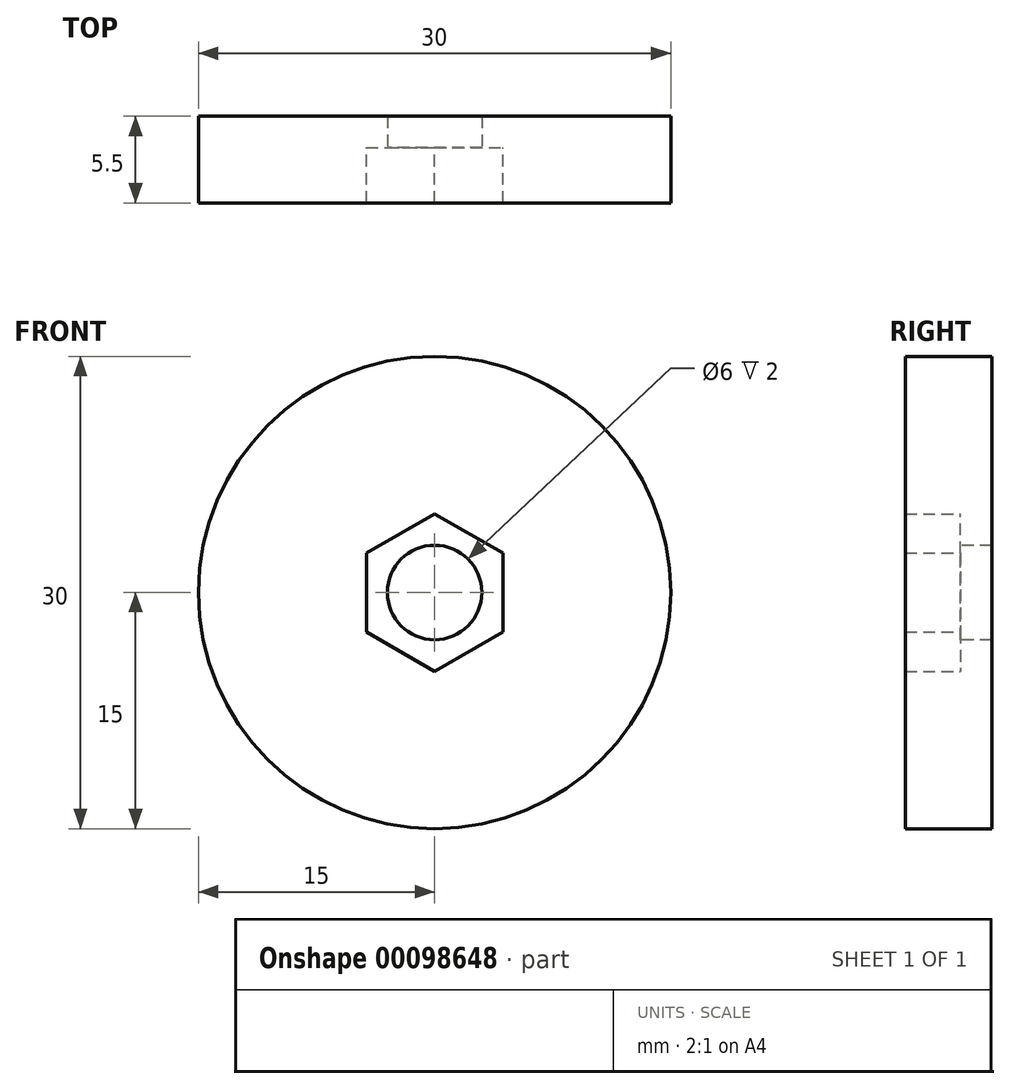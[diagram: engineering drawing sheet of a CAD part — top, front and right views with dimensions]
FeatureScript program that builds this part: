
annotation { "Feature Type Name" : "Feature", "Feature Type Description" : "" }
export const myFeature = defineFeature(function(context is Context, id is Id, definition is map)
    precondition{}
    {
        {
            var Q0;
            Q0=qCreatedBy(makeId("Front.planeOp"),FACE);
            var sketch = newSketch(context, id + "F0", { "sketchPlane" : qUnion([Q0])});
            skCircle(sketch, "E0", {"center": v(0, 0) * mm, "radius": 15 * mm});
            skCircle(sketch, "E1.cCircle", {"center": v(0, 0) * mm, "radius": 5 * mm, "construction": true});
            skLineSegment(sketch, "E1.0", {"start": v(0, 5) * mm, "end": v(4.33, 2.5) * mm});
            skLineSegment(sketch, "E1.1", {"start": v(4.33, 2.5) * mm, "end": v(4.33, -2.5) * mm});
            skLineSegment(sketch, "E1.2", {"start": v(4.33, -2.5) * mm, "end": v(0, -5) * mm});
            skLineSegment(sketch, "E1.3", {"start": v(0, -5) * mm, "end": v(-4.33, -2.5) * mm});
            skLineSegment(sketch, "E1.4", {"start": v(-4.33, -2.5) * mm, "end": v(-4.33, 2.5) * mm});
            skLineSegment(sketch, "E1.5", {"start": v(-4.33, 2.5) * mm, "end": v(0, 5) * mm});
            skCircle(sketch, "E2", {"center": v(0, 0) * mm, "radius": 3 * mm});
            skSolve(sketch);
        }
        {
            var Q0;
            Q0=makeQuery(id+"F0.imprint","IMPRINT",FACE,{"disambiguationData":[TD([[makeQuery(id+"F0.imprint","IMPRINT",EDGE,{"derivedFrom":sQuery(id+"F0.wireOp",EDGE,"E0")}),1.0]])]});
            extrude(context, id + "F1", {"entities" : qUnion([Q0]), "depth" : 3.5 * mm});
        }
        {
            var Q0;
            Q0=makeQuery(id+"F0.imprint","IMPRINT",FACE,{"disambiguationData":[TD([[makeQuery(id+"F0.imprint","IMPRINT",EDGE,{"derivedFrom":sQuery(id+"F0.wireOp",EDGE,"E0")}),1.0]])]});
            var Q1;
            Q1=makeQuery(id+"F0.imprint","IMPRINT",FACE,{"disambiguationData":[TD([[makeQuery(id+"F0.imprint","IMPRINT",EDGE,{"derivedFrom":sQuery(id+"F0.wireOp",EDGE,"E1.0")}),-1.0]])]});
            extrude(context, id + "F2", {"entities" : qUnion([Q0, Q1]), "operationType" : NewBodyOperationType.ADD, "oppositeDirection" : true, "depth" : 2 * mm});
        }
    });
